# Revit family: Quiet-SqrTop_RndBase
name_source: partatom
category: Furniture
revit_build: Autodesk Revit 2016 (Build: 20150714_1515(x64)
units: mm (PartAtom-declared; Revit-internal decimal feet)

## family parameters
Always vertical = Yes
Cut with Voids When Loaded = No
OmniClass Number = 23.40.20.14.14.17
OmniClass Title = Stools
Room Calculation Point = No
Shared = No
Work Plane-Based = No

## types (15) — shared parameters
Manufacturer = Bernhardt Design
URL = http://bernhardtdesign.com

## per-type parameters (varying)
| type | Base Width | Catalog | Column Radius | Depth | Height | SKU | Width |
| Quiet - QUS-183 18" sqr top/ rnd base occasional | 14" | QUS-183 | 3/8" | 18" | 18" | QUS-183 | 18" |
| Quiet - QUS-223 22" sqr top/ rnd base occasional | 17 1/2" | QUS-223 | 3/8" | 22" | 18" | QUS-223 | 22" |
| Quiet - QUS-303 30" sqr top/ rnd base occasional | 20 7/8" | QUS-303 | 1 1/2" | 30" | 13" | QUS-303 | 30" |
| Quiet - QUS-363 36" sqr top/ rnd base occasional | 20 7/8" | QUS-363 | 1 1/2" | 36" | 13" | QUS-363 | 36" |
| Quiet - QUS-423 42" sqr top/ rnd base occasional | 24" | QUS-423 | 1 1/2" | 42" | 13" | QUS-423 | 42" |
| Quiet - QUS-187 18" sqr top/ rnd base mid | 14" | QUS-187 | 7/16" | 18" | 23 3/4" | QUS-187 | 18" |
| Quiet - QUS-227 22" sqr top/ rnd base mid | 17 1/2" | QUS-227 | 7/16" | 22" | 23 3/4" | QUS-227 | 22" |
| Quiet - QUS-307 30" sqr top/ rnd base mid | 20 7/8" | QUS-307 | 1 1/2" | 30" | 23 3/4" | QUS-307 | 30" |
| Quiet - QUS-367 36" sqr top/ rnd base mid | 20 7/8" | QUS-367 | 1 1/2" | 36" | 23 3/4" | QUS-367 | 36" |
| Quiet - QUS-427 42" sqr top/ rnd base mid | 24" | QUS-427 | 1 1/2" | 42" | 23 3/4" | QUS-427 | 42" |
| Quiet - QUS-311 30" sqr top/ rnd base conference | 20 7/8" | QUS-311 | 1 1/2" | 30" | 29" | QUS-311 | 30" |
| Quiet - QUS-371 36" sqr top/ rnd base conference | 20 7/8" | QUS-371 | 1 1/2" | 36" | 29" | QUS-371 | 36" |
| Quiet - QUS-431 42" sqr top/ rnd base conference | 24" | QUS-431 | 1 1/2" | 42" | 29" | QUS-431 | 42" |
| Quiet - QUS-273 27" sqr top/ rnd base bar | 20 7/8" | QUS-273 | 1 1/2" | 27" | 42" | QUS-273 | 27" |
| Quiet - QUS-315 30" sqr top/ rnd base bar | 20 7/8" | QUS-315 | 1 1/2" | 30" | 42" | QUS-315 | 30" |

## geometry (parser evidence)
native form markers: Blend x2, Sweep x2
no freeform markers — native parametric forms only
